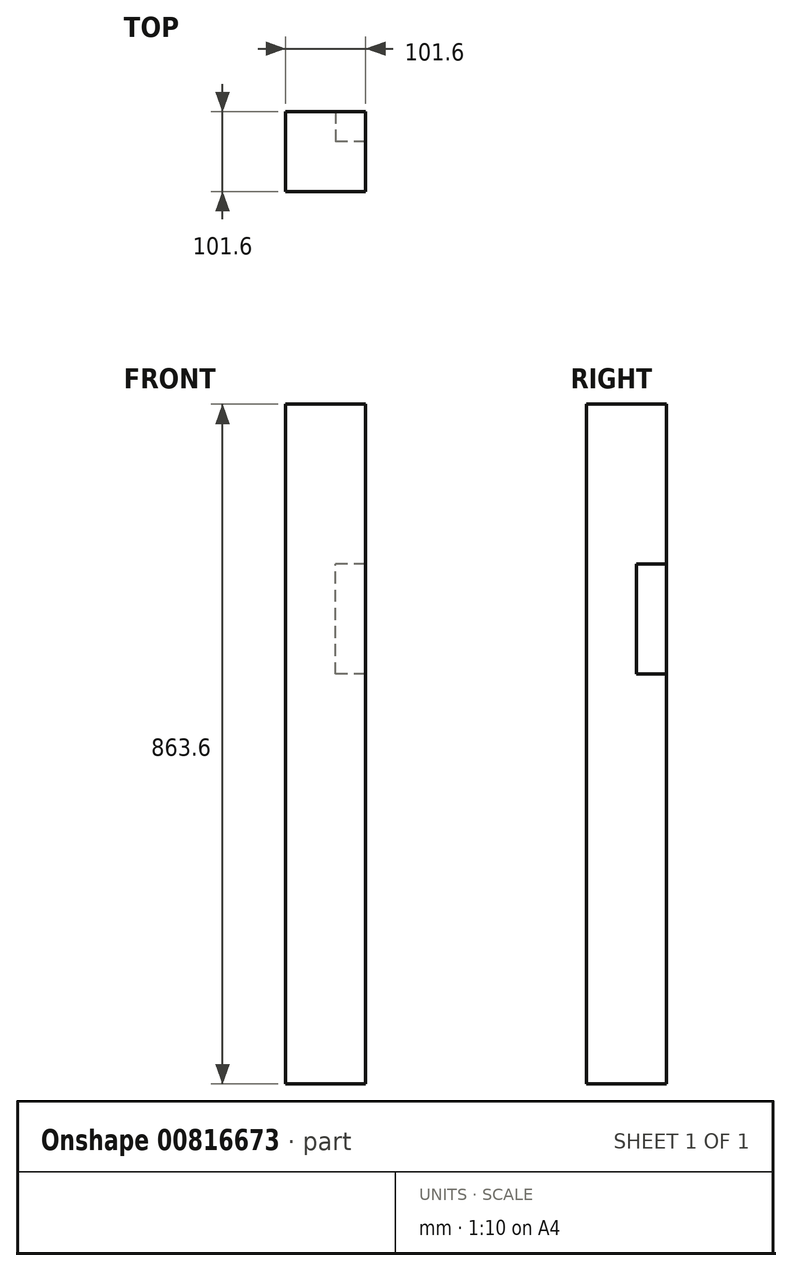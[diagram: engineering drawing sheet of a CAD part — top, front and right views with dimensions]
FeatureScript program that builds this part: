
annotation { "Feature Type Name" : "Feature", "Feature Type Description" : "" }
export const myFeature = defineFeature(function(context is Context, id is Id, definition is map)
    precondition{}
    {
        {
            var Q0;
            Q0=qCreatedBy(makeId("Front.planeOp"),FACE);
            var sketch = newSketch(context, id + "F0", { "sketchPlane" : qUnion([Q0])});
            skLineSegment(sketch, "E0.bottom", {"start": v(-96.14, -67.6) * mm, "end": v(5.46, -67.6) * mm});
            skLineSegment(sketch, "E0.top", {"start": v(-96.14, 796) * mm, "end": v(5.46, 796) * mm});
            skLineSegment(sketch, "E0.left", {"start": v(-96.14, -67.6) * mm, "end": v(-96.14, 796) * mm});
            skLineSegment(sketch, "E0.right", {"start": v(5.46, -67.6) * mm, "end": v(5.46, 796) * mm});
            skLineSegment(sketch, "E1.bottom", {"start": v(5.46, 453.1) * mm, "end": v(-32.64, 453.1) * mm});
            skLineSegment(sketch, "E1.top", {"start": v(5.46, 592.8) * mm, "end": v(-32.64, 592.8) * mm});
            skLineSegment(sketch, "E1.left", {"start": v(5.46, 453.1) * mm, "end": v(5.46, 592.8) * mm});
            skLineSegment(sketch, "E1.right", {"start": v(-32.64, 453.1) * mm, "end": v(-32.64, 592.8) * mm});
            skSolve(sketch);
        }
        {
            var Q0;
            {var subQ1=sQuery(id+"F0.wireOp",EDGE,"E0.bottom");Q0=makeQuery(id+"F0.imprint","IMPRINT",FACE,{"disambiguationData":[TD([[makeQuery(id+"F0.imprint","IMPRINT",EDGE,{"derivedFrom":subQ1}),1.0]])]});}
            extrude(context, id + "F1", {"entities" : qUnion([Q0]), "oppositeDirection" : true, "depth" : 101.6 * mm, "offsetDistance" : 25.4 * mm});
        }
        {
            var Q0;
            {var subQ2=sQuery(id+"F0.wireOp",EDGE,"E1.bottom");Q0=makeQuery(id+"F0.imprint","IMPRINT",FACE,{"disambiguationData":[TD([[makeQuery(id+"F0.imprint","IMPRINT",EDGE,{"derivedFrom":subQ2}),-1.0]])]});}
            extrude(context, id + "F2", {"entities" : qUnion([Q0]), "operationType" : NewBodyOperationType.ADD, "oppositeDirection" : true, "depth" : 63.5 * mm, "offsetDistance" : 25.4 * mm});
        }
    });
